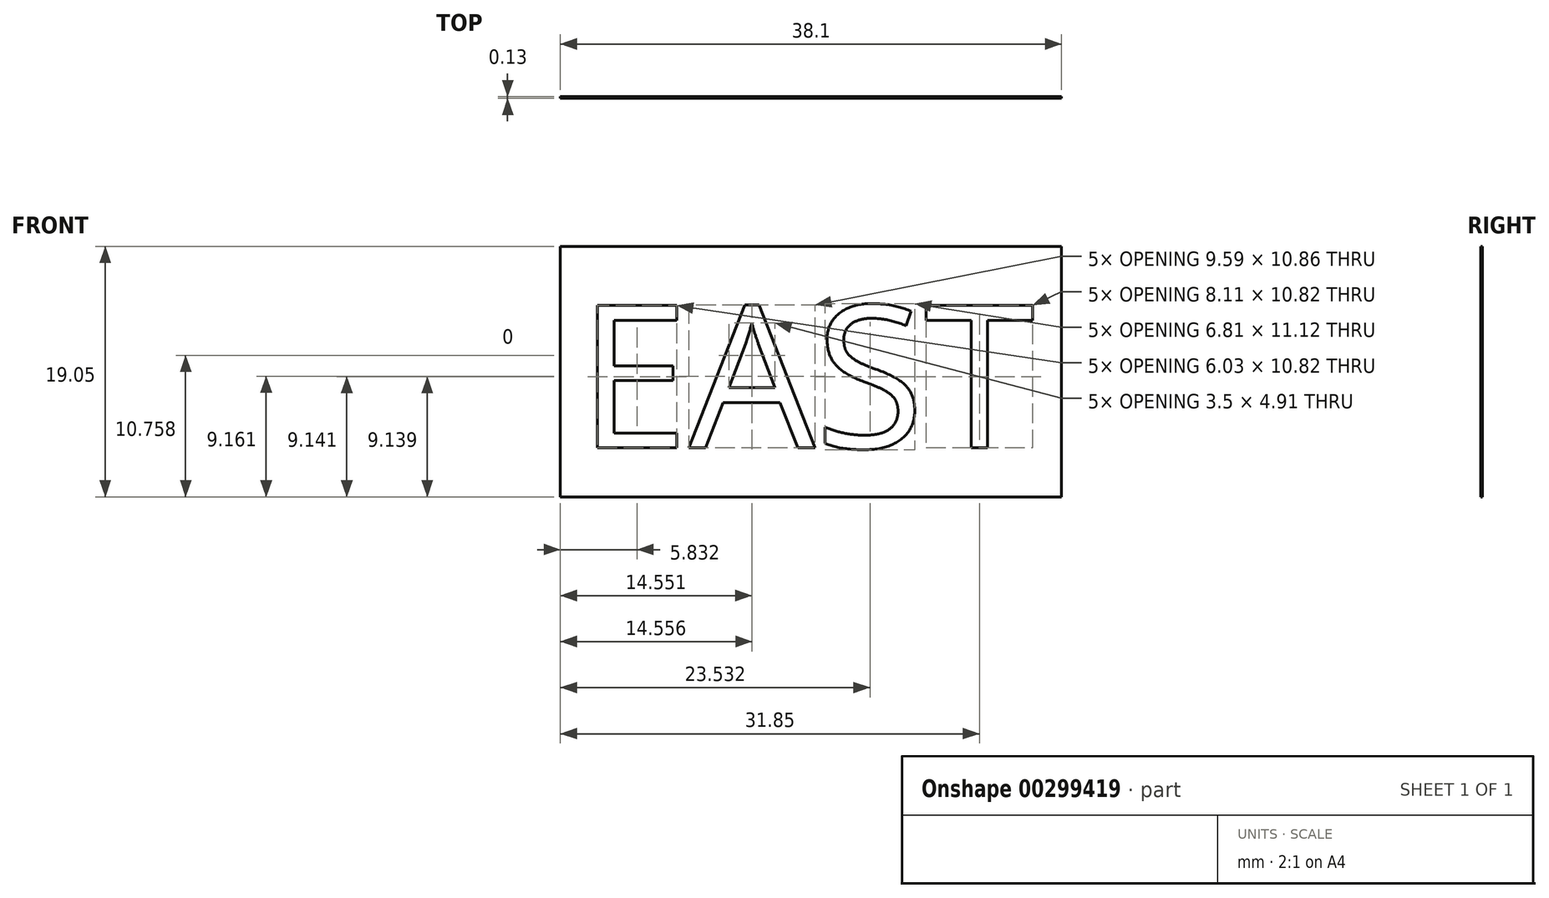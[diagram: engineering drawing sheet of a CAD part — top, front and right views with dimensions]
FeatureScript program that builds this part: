
annotation { "Feature Type Name" : "Feature", "Feature Type Description" : "" }
export const myFeature = defineFeature(function(context is Context, id is Id, definition is map)
    precondition{}
    {
        {
            var Q0;
            Q0=qCreatedBy(makeId("Front.planeOp"),FACE);
            var sketch = newSketch(context, id + "F0", { "sketchPlane" : qUnion([Q0])});
            skLineSegment(sketch, "E0.bottom", {"start": v(0, 0) * mm, "end": v(38.1, 0) * mm});
            skLineSegment(sketch, "E0.top", {"start": v(0, 19.05) * mm, "end": v(38.1, 19.05) * mm});
            skLineSegment(sketch, "E0.left", {"start": v(0, 0) * mm, "end": v(0, 19.05) * mm});
            skLineSegment(sketch, "E0.right", {"start": v(38.1, 0) * mm, "end": v(38.1, 19.05) * mm});
            skSolve(sketch);
        }
        {
            var Q0;
            Q0=makeQuery(id+"F0.imprint","IMPRINT",FACE,{"disambiguationData":[TD([[makeQuery(id+"F0.imprint","IMPRINT",EDGE,{"derivedFrom":sQuery(id+"F0.wireOp",EDGE,"E0.bottom")}),1.0]])]});
            extrude(context, id + "F1", {"entities" : qUnion([Q0]), "depth" : 0.13 * mm});
        }
        {
            var Q0;
            Q0=makeQuery(id+"F1.opExtrude","CAP_FACE",FACE,{"disambiguationData":[OSD([sQuery(id+"F0.wireOp",EDGE,"E0.bottom"),sQuery(id+"F0.wireOp",EDGE,"E0.top"),sQuery(id+"F0.wireOp",EDGE,"E0.left"),sQuery(id+"F0.wireOp",EDGE,"E0.right")])],"isStart":false});
            var sketch = newSketch(context, id + "F2", { "sketchPlane" : qUnion([Q0])});
            skText(sketch, "E1", { "text": "EAST", "fontName": "OpenSans-Regular.ttf"});
            const initialGuessF2  = {"E1": [0.00133, 0.00373, 1, 0, 0.01091]};
            skSetInitialGuess(sketch, initialGuessF2);
            skSolve(sketch);
        }
        {
            var Q0;
            Q0 = qSketchRegion(id + "F2", true);
            extrude(context, id + "F3", {"entities" : qUnion([Q0]), "operationType" : NewBodyOperationType.REMOVE, "oppositeDirection" : true, "depth" : 0.05 * mm});
        }
    });
